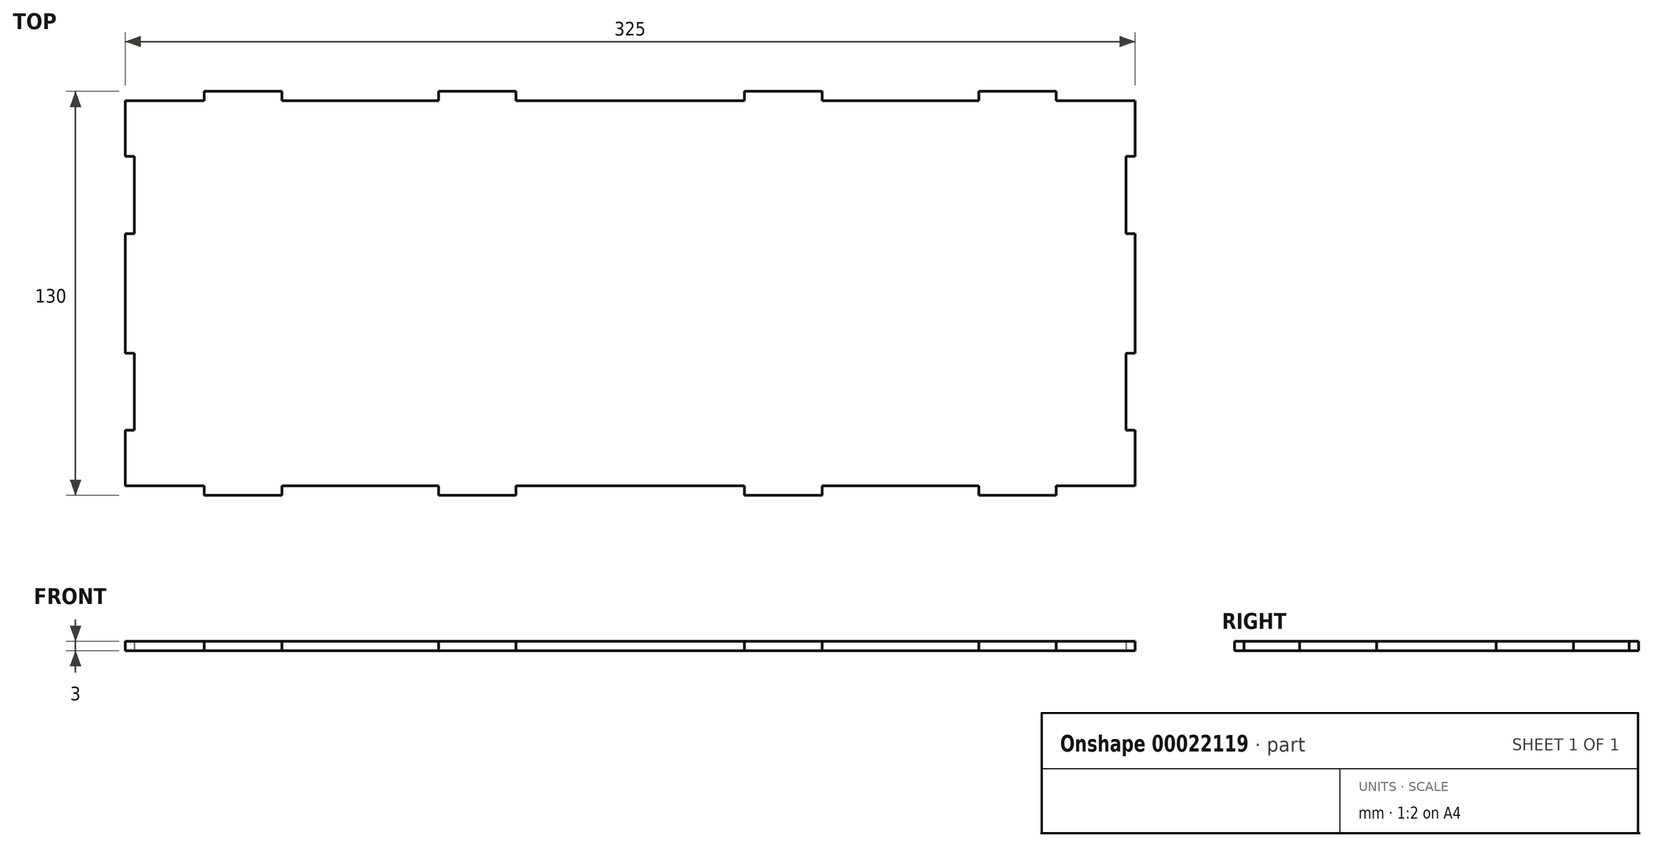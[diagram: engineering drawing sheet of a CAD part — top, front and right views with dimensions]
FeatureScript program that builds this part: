
annotation { "Feature Type Name" : "Feature", "Feature Type Description" : "" }
export const myFeature = defineFeature(function(context is Context, id is Id, definition is map)
    precondition{}
    {
        {
            var Q0;
            Q0=qCreatedBy(makeId("Top.planeOp"),FACE);
            var sketch = newSketch(context, id + "F0", { "sketchPlane" : qUnion([Q0])});
            skLineSegment(sketch, "E0", {"start": v(0, 5) * mm, "end": v(0, -125) * mm, "construction": true});
            skLineSegment(sketch, "E1.left", {"start": v(-137.13, 5) * mm, "end": v(-137.13, 2) * mm});
            skLineSegment(sketch, "E1.right", {"start": v(-112.13, 5) * mm, "end": v(-112.13, 2) * mm});
            skLineSegment(sketch, "E2.left", {"start": v(-61.72, 5) * mm, "end": v(-61.72, 2) * mm});
            skLineSegment(sketch, "E2.right", {"start": v(-36.72, 5) * mm, "end": v(-36.72, 2) * mm});
            skLineSegment(sketch, "E3.MirrorCS", {"start": v(61.72, 5) * mm, "end": v(61.72, 2) * mm});
            skLineSegment(sketch, "E4.MirrorCS", {"start": v(36.72, 5) * mm, "end": v(36.72, 2) * mm});
            skLineSegment(sketch, "E5.MirrorCS", {"start": v(137.13, 5) * mm, "end": v(137.13, 2) * mm});
            skLineSegment(sketch, "E6.MirrorCS", {"start": v(112.13, 5) * mm, "end": v(112.13, 2) * mm});
            skLineSegment(sketch, "E7.MirrorCS", {"start": v(-137.13, -125) * mm, "end": v(-137.13, -122) * mm});
            skLineSegment(sketch, "E8.MirrorCS", {"start": v(-112.13, -125) * mm, "end": v(-112.13, -122) * mm});
            skLineSegment(sketch, "E9.MirrorCS", {"start": v(-61.72, -125) * mm, "end": v(-61.72, -122) * mm});
            skLineSegment(sketch, "E10.MirrorCS", {"start": v(-36.72, -125) * mm, "end": v(-36.72, -122) * mm});
            skLineSegment(sketch, "E11.MirrorCS", {"start": v(36.72, -125) * mm, "end": v(36.72, -122) * mm});
            skLineSegment(sketch, "E12.MirrorCS", {"start": v(61.72, -125) * mm, "end": v(61.72, -122) * mm});
            skLineSegment(sketch, "E13.MirrorCS", {"start": v(112.13, -125) * mm, "end": v(112.13, -122) * mm});
            skLineSegment(sketch, "E14.MirrorCS", {"start": v(137.13, -125) * mm, "end": v(137.13, -122) * mm});
            skLineSegment(sketch, "E15", {"start": v(-162.5, 2) * mm, "end": v(-162.5, -15.9) * mm});
            skLineSegment(sketch, "E16", {"start": v(162.5, 2) * mm, "end": v(162.5, -15.9) * mm});
            skLineSegment(sketch, "E17", {"start": v(-162.5, -60) * mm, "end": v(162.5, -60) * mm, "construction": true});
            skLineSegment(sketch, "E18", {"start": v(-162.5, -122) * mm, "end": v(-137.13, -122) * mm});
            skLineSegment(sketch, "E19", {"start": v(137.13, -125) * mm, "end": v(112.13, -125) * mm});
            skLineSegment(sketch, "E20", {"start": v(61.72, -125) * mm, "end": v(36.72, -125) * mm});
            skLineSegment(sketch, "E21", {"start": v(-36.72, -125) * mm, "end": v(-61.72, -125) * mm});
            skLineSegment(sketch, "E22", {"start": v(-112.13, -125) * mm, "end": v(-137.13, -125) * mm});
            skLineSegment(sketch, "E23.trimOffspring", {"start": v(-112.13, -122) * mm, "end": v(-61.72, -122) * mm});
            skLineSegment(sketch, "E24.trimOffspring", {"start": v(-36.72, -122) * mm, "end": v(36.72, -122) * mm});
            skLineSegment(sketch, "E25.trimOffspring", {"start": v(61.72, -122) * mm, "end": v(112.13, -122) * mm});
            skLineSegment(sketch, "E26.trimOffspring", {"start": v(137.13, -122) * mm, "end": v(162.5, -122) * mm});
            skPoint(sketch, "E27.MirrorCS.end.orphan", {"position": v(36.72, 2) * mm});
            skPoint(sketch, "E27.MirrorCS.start.orphan", {"position": v(61.72, 2) * mm});
            skPoint(sketch, "E28.MirrorCS.end.orphan", {"position": v(112.13, 2) * mm});
            skPoint(sketch, "E28.MirrorCS.start.orphan", {"position": v(137.13, 2) * mm});
            skLineSegment(sketch, "E29", {"start": v(137.13, 2) * mm, "end": v(162.5, 2) * mm});
            skLineSegment(sketch, "E30", {"start": v(137.13, 5) * mm, "end": v(112.13, 5) * mm});
            skLineSegment(sketch, "E31", {"start": v(112.13, 2) * mm, "end": v(61.72, 2) * mm});
            skLineSegment(sketch, "E32", {"start": v(61.72, 5) * mm, "end": v(36.72, 5) * mm});
            skLineSegment(sketch, "E33", {"start": v(36.72, 2) * mm, "end": v(-36.72, 2) * mm});
            skLineSegment(sketch, "E34", {"start": v(-36.72, 5) * mm, "end": v(-61.72, 5) * mm});
            skLineSegment(sketch, "E35", {"start": v(-61.72, 2) * mm, "end": v(-112.13, 2) * mm});
            skLineSegment(sketch, "E36", {"start": v(-112.13, 5) * mm, "end": v(-137.13, 5) * mm});
            skLineSegment(sketch, "E37", {"start": v(-137.13, 2) * mm, "end": v(-162.5, 2) * mm});
            skLineSegment(sketch, "E38.bottom", {"start": v(162.5, -15.9) * mm, "end": v(159.57, -15.9) * mm});
            skLineSegment(sketch, "E38.top", {"start": v(162.5, -40.76) * mm, "end": v(159.5, -40.76) * mm});
            skLineSegment(sketch, "E38.right", {"start": v(159.57, -15.9) * mm, "end": v(159.57, -40.76) * mm});
            skLineSegment(sketch, "E39.MirrorCS", {"start": v(159.57, -104.1) * mm, "end": v(159.57, -79.24) * mm});
            skLineSegment(sketch, "E40.MirrorCS", {"start": v(162.5, -79.24) * mm, "end": v(159.5, -79.24) * mm});
            skLineSegment(sketch, "E41.MirrorCS", {"start": v(162.5, -104.1) * mm, "end": v(159.57, -104.1) * mm});
            skLineSegment(sketch, "E42.trimOffspring", {"start": v(162.5, -104.1) * mm, "end": v(162.5, -122) * mm});
            skLineSegment(sketch, "E43.trimOffspring", {"start": v(162.5, -40.76) * mm, "end": v(162.5, -79.24) * mm});
            skLineSegment(sketch, "E44.MirrorCS", {"start": v(-159.57, -15.9) * mm, "end": v(-159.57, -40.76) * mm});
            skLineSegment(sketch, "E45.MirrorCS", {"start": v(-159.57, -104.1) * mm, "end": v(-159.57, -79.24) * mm});
            skLineSegment(sketch, "E46.MirrorCS", {"start": v(-162.5, -40.76) * mm, "end": v(-159.5, -40.76) * mm});
            skLineSegment(sketch, "E47.MirrorCS", {"start": v(-162.5, -15.9) * mm, "end": v(-159.57, -15.9) * mm});
            skLineSegment(sketch, "E48.MirrorCS", {"start": v(-162.5, -79.24) * mm, "end": v(-159.5, -79.24) * mm});
            skLineSegment(sketch, "E49.MirrorCS", {"start": v(-162.5, -104.1) * mm, "end": v(-159.57, -104.1) * mm});
            skLineSegment(sketch, "E50.trimOffspring", {"start": v(-162.5, -40.76) * mm, "end": v(-162.5, -79.24) * mm});
            skLineSegment(sketch, "E51.trimOffspring", {"start": v(-162.5, -104.1) * mm, "end": v(-162.5, -122) * mm});
            skSolve(sketch);
        }
        {
            var Q0;
            Q0=makeQuery(id+"F0.imprint","IMPRINT",FACE,{"disambiguationData":[TD([[makeQuery(id+"F0.imprint","IMPRINT",EDGE,{"derivedFrom":sQuery(id+"F0.wireOp",EDGE,"E1.left")}),1.0]])]});
            extrude(context, id + "F1", {"entities" : qUnion([Q0]), "depth" : 3 * mm});
        }
    });
